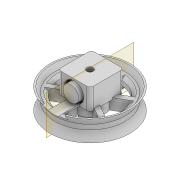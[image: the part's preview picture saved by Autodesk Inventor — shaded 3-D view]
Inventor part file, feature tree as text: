
AUTODESK INVENTOR PART (.ipt)
format: ipt  version: 2022 (Build 260153000, 153)  size: 479,232 bytes
history: native  units: mm
features: extrude x14, sketch x13, projected_geometry x11, chamfer x5, thicken_offset x2, plane x1, fillet x1
ambient origin geometry x8: Origin, YZ Plane, XZ Plane, XY Plane, X Axis, Y Axis, Z Axis, Center Point
bodies: Solid1 (feature_tree)
feature tree (47):
  extrude  "Extrusion1"  Depth=12.2mm
  extrude  "Extrusion2"  Depth=1.0mm
  extrude  "Extrusion3"  Depth=2.0mm TaperAngle=0.0deg
  plane  "Work Plane1"
  extrude  "Extrusion12"  Depth=10.0mm
  fillet  "Fillet5"  Radius=10.0mm
  extrude  "Extrusion14"  Depth=2.0mm
  extrude  "Extrusion15"  Depth=5.0mm TaperAngle=0.0deg
  extrude  "Extrusion16"  Depth=4.1mm
  extrude  "Extrusion17"  Depth=9.0mm
  sketch  "Sketch19"  dims[d79=3.0mm d80=2.0mm]
  extrude  "Extrusion18"  Depth=2.0mm
  extrude  "Extrusion19"  Depth=2.0mm
  thicken_offset  "Thicken1"
  extrude  "Extrusion20"  Depth=3.0mm TaperAngle=0.0deg
  extrude  "Extrusion21"  Depth=1.0mm
  chamfer  "Chamfer1"  Distance=2.0mm
  chamfer  "Chamfer2"  Distance=3.0mm
  chamfer  "Chamfer3"  Distance=2.0mm
  chamfer  "Chamfer4"  Distance=3.0mm
  sketch  "Sketch22"  dims[d86=4.1mm d87=2.0mm d88=3.0mm d89=2.0mm d90=3.0mm d91=2.4mm d92=0.0mm d94=17.0mm d95=2.0mm d96=0.0mm d97=1.5mm d98=2.0mm d99=0.0mm d100=100.0mm d101=0.0mm d102=12.0mm d103=12.0mm d104=3.0mm d105=3.0mm d106=0.0mm d107=3.0mm d108=8.0mm d109=8.0mm d110=3.0mm d111=0.0mm d112=3.0mm d113=5.0mm d114=45.0deg d115=3.0mm d116=5.0mm d117=45.0deg d118=2.0mm d119=3.0mm d120=45.0deg d121=2.0mm d122=3.0mm d123=45.0deg d124=37.0mm d125=19.0mm d126=1.5mm d127=1.5mm d128=30.0mm d130=360.0deg d132=6.0mm d133=0.0mm d134=8.0mm d135=0.0mm d136=2.0mm d137=2.0mm d138=45.0deg d139=2.0mm d140=2.0mm]
  extrude  "Extrusion22"  Depth=2.4mm TaperAngle=0.0deg
  extrude  "Extrusion23"  Depth=17.0mm
  chamfer  "Chamfer5"  Distance=2.0mm
  thicken_offset  "Thicken2"
  sketch  "Sketch1"  dims[d0=9.8mm d1=12.2mm]
  sketch  "Sketch2"  dims[d3=4.0mm d4=1.0mm]
  projected_geometry  "Projected Loop1"
  sketch  "Sketch3"  dims[d5=18.0mm d6=0.0mm d7=2.0mm d8=0.0mm]
  projected_geometry  "Projected Loop2"
  sketch  "Sketch6"  dims[d9=3.0mm d10=0.0mm d49=4.1mm d50=10.0mm]
  projected_geometry  "Projected Loop3"
  projected_geometry  "Projected Loop4"
  sketch  "Sketch14"  dims[d63=100.0mm d64=0.0mm d65=2.0mm]
  sketch  "Sketch15"  dims[d69=7.0mm d71=5.0mm d72=0.0mm]
  projected_geometry  "Projected Loop10"
  projected_geometry  "Projected Loop11"
  sketch  "Sketch16"  dims[d73=16.0mm d74=4.1mm]
  projected_geometry  "Projected Loop12"
  sketch  "Sketch17"  dims[d75=1.4mm d76=9.0mm]
  sketch  "Sketch18"  dims[d77=1.0mm d78=2.0mm]
  projected_geometry  "Projected Loop13"
  projected_geometry  "Projected Loop14"
  projected_geometry  "Projected Loop15"
  sketch  "Sketch20"  dims[d81=4.0mm d82=3.0mm d83=0.0mm]
  sketch  "Sketch21"  dims[d84=1.4mm d85=1.0mm]
  projected_geometry  "Projected Loop16"
